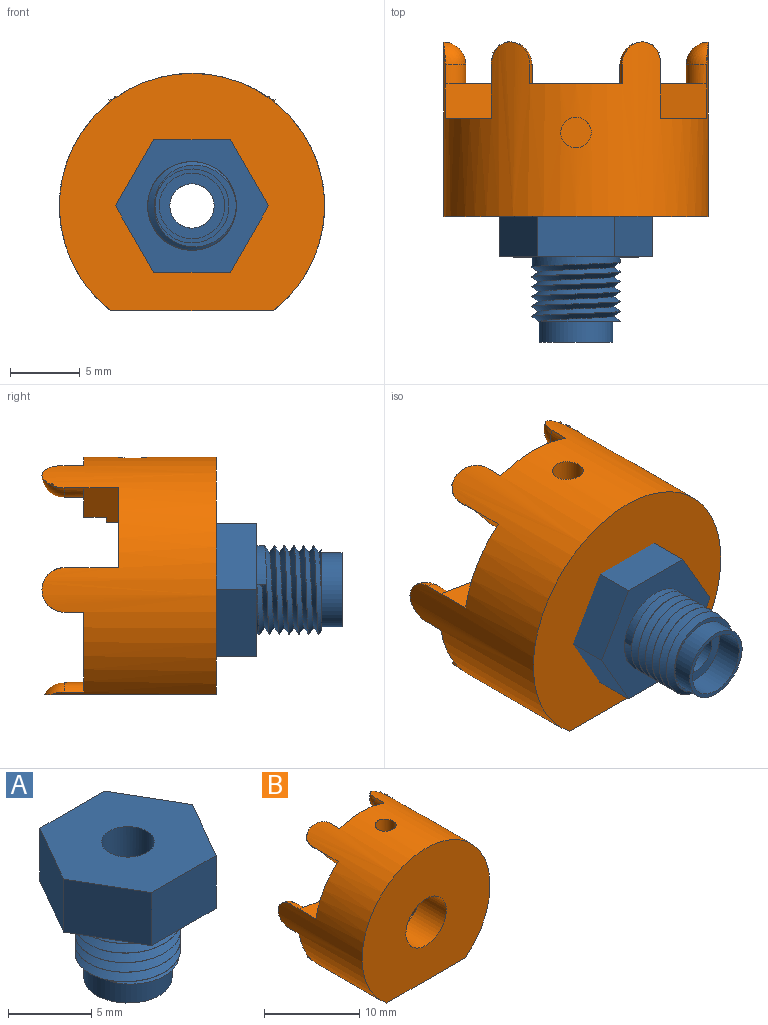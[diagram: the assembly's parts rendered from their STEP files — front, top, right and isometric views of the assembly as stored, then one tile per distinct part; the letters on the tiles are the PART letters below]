
ASSEMBLY  parts=2 mates=2
PART A: 18 faces, bbox 11.4x9.9x10.4 mm
  f0: cylinder r=3.17mm len=6.35mm, axis (0,0,1), area 14.5mm2, adj f3,f13,f15,f16,f17
  f1: cylinder r=1.59mm len=8mm, axis (0,0,-1), area 79.8mm2, adj f4,f12
  f2: plane 5.3x5.3mm, normal (0,0,-1), area 4.7mm2, adj f11,f14
  f3: plane 10.97x9.5mm, normal (0,0,-1), area 46.5mm2, adj f0,f5,f6,f7,f8,f9,f10
  f4: plane 10.97x9.5mm, normal (0,0,1), area 70.2mm2, adj f1,f5,f6,f7,f8,f9,f10
  f5: plane 4.75x3.9mm, normal (-0.87,0.5,0), area 21.4mm2, adj f3,f4,f6,f10
  f6: plane 4.75x3.9mm, normal (-0.87,-0.5,0), area 21.4mm2, adj f3,f4,f5,f7
  f7: plane 5.48x3.9mm, normal (0,-1,0), area 21.4mm2, adj f3,f4,f6,f8
  f8: plane 4.75x3.9mm, normal (0.87,-0.5,0), area 21.4mm2, adj f3,f4,f7,f9
  f9: plane 4.75x3.9mm, normal (0.87,0.5,0), area 21.4mm2, adj f3,f4,f8,f10
  f10: plane 5.48x3.9mm, normal (0,1,0), area 21.4mm2, adj f3,f4,f5,f9
  f11: cylinder r=2.35mm len=4.7mm, axis (0,0,-1), area 29.5mm2, adj f2,f12
  f12: plane 4.7x4.7mm, normal (0,0,-1), area 9.4mm2, adj f1,f11
  f13: plane 6.3x6.29mm, normal (0,0,-1), area 4.9mm2, adj f0,f14,f16,f17
  f14: cylinder r=2.65mm len=5.3mm, axis (0,0,-1), area 25mm2, adj f2,f13
  f15: plane 0.7x0.5mm, normal (-0.13,0.99,0), area 0.2mm2, adj f0,f16,f17
  f16: bspline ~7.33x6.35mm, area 71mm2, adj f0,f13,f15,f17
  f17: bspline ~6.35x6.35mm, area 64.2mm2, adj f0,f13,f15,f16
PART B: 36 faces, bbox 19x12.5x17 mm
  f0: plane 9.7x3.9mm, normal (0,0,-1), area 32.5mm2, adj f5,f7,f9,f27,f28,f30,f31,f33
  f1: cylinder r=9.5mm len=19mm, axis (0,-1,0), area 439.5mm2, adj f2,f3,f12,f13,f14,f15,f16,f17
  f2: plane 11.78x4.3mm, normal (0,1,0), area 32.3mm2, adj f1,f4,f16,f17,f28,f31
  f3: plane 18.73x9.05mm, normal (0,1,0), area 65.6mm2, adj f1,f8,f10,f13,f14,f15,f18,f25
  f4: plane 8.62x1.6mm, normal (0,0,-1), area 13.8mm2, adj f2,f5,f28,f31
  f5: plane 8.62x0.35mm, normal (0,1,0), area 2.9mm2, adj f0,f4,f28,f31
  f6: plane 11.3x6.16mm, normal (0,1,0), area 13.1mm2, adj f7,f8,f9,f10,f11,f26,f29,f32
  f7: plane 9.7x3.9mm, normal (-1,0,0), area 34.2mm2, adj f0,f6,f11,f32,f33,f34
  f8: plane 6.16x1.6mm, normal (-1,0,0), area 9.9mm2, adj f3,f6,f26,f32
  f9: plane 9.7x3.9mm, normal (1,0,0), area 34.2mm2, adj f0,f6,f11,f29,f30,f34
  f10: plane 6.16x1.6mm, normal (1,0,0), area 9.9mm2, adj f3,f6,f26,f29
  f11: plane 9.7x3.9mm, normal (0,0,1), area 37.8mm2, adj f6,f7,f9,f34
  f12: plane 19x17mm, normal (0,-1,0), area 239.3mm2, adj f1,f25,f35
  f13: cylinder r=1.6mm len=2.74mm, axis (0,-1,0), area 4.6mm2, adj f1,f3,f23,f25
  f14: cylinder r=1.6mm len=2.74mm, axis (0,-1,0), area 4.6mm2, adj f1,f3,f22,f25
  f15: cylinder r=1.6mm len=3.19mm, axis (0,-1,0), area 6.7mm2, adj f1,f3,f19,f32
  f16: cylinder r=1.6mm len=2.91mm, axis (0,-1,0), area 6.7mm2, adj f1,f2,f20,f31
  f17: cylinder r=1.6mm len=2.91mm, axis (0,-1,0), area 6.7mm2, adj f1,f2,f21,f28
  f18: cylinder r=1.6mm len=3.19mm, axis (0,-1,0), area 6.7mm2, adj f1,f3,f24,f29
  f19: sphere r=1.6mm, area 5mm2, adj f1,f15
  f20: sphere r=1.6mm, area 7.7mm2, adj f1,f16
  f21: sphere r=1.6mm, area 7.7mm2, adj f1,f17
  f22: sphere r=1.6mm, area 4.3mm2, adj f1,f14,f25
  f23: sphere r=1.6mm, area 4.3mm2, adj f1,f13,f25
  f24: sphere r=1.6mm, area 5mm2, adj f1,f18
  f25: plane 12.33x11.66mm, normal (0,0,-1), area 123.7mm2, adj f1,f3,f12,f13,f14,f22,f23
  f26: plane 11.3x1.6mm, normal (0,0,1), area 18.1mm2, adj f3,f6,f8,f10
  f27: cylinder r=1.1mm len=4.59mm, axis (0,0,-1), area 31.7mm2, adj f0,f1
  f28: plane 2.51x2.47mm, normal (-0.77,0,-0.64), area 7.3mm2, adj f0,f1,f2,f4,f5,f17,f30
  f29: plane 4.53x2.51mm, normal (0.17,0,0.99), area 10.2mm2, adj f1,f3,f6,f9,f10,f18,f30
  f30: plane 6.49x5.34mm, normal (0,1,0), area 20.3mm2, adj f0,f1,f9,f28,f29
  f31: plane 2.51x2.47mm, normal (0.77,0,-0.64), area 7.3mm2, adj f0,f1,f2,f4,f5,f16,f33
  f32: plane 4.53x2.51mm, normal (-0.17,0,0.99), area 10.2mm2, adj f1,f3,f6,f7,f8,f15,f33
  f33: plane 6.49x5.34mm, normal (0,1,0), area 20.3mm2, adj f0,f1,f7,f31,f32
  f34: plane 9.7x9.7mm, normal (0,1,0), area 65.8mm2, adj f0,f7,f9,f11,f35
  f35: cylinder r=3mm len=6mm, axis (0,-1,0), area 75.4mm2, adj f12,f34
PLACE A rot(axis=(-1,0,0),90deg) t=(40.27,1,13.68)mm
PLACE B t=(34.78,0,13.68)mm
MATE parallel A.f4 <-> B.f12  axis (0,1,0) through (32.04,1,18.42)mm
MATE cylindrical A.f0 <-> B.f35  axis (0,1,0) through (34.78,1,13.68)mm
